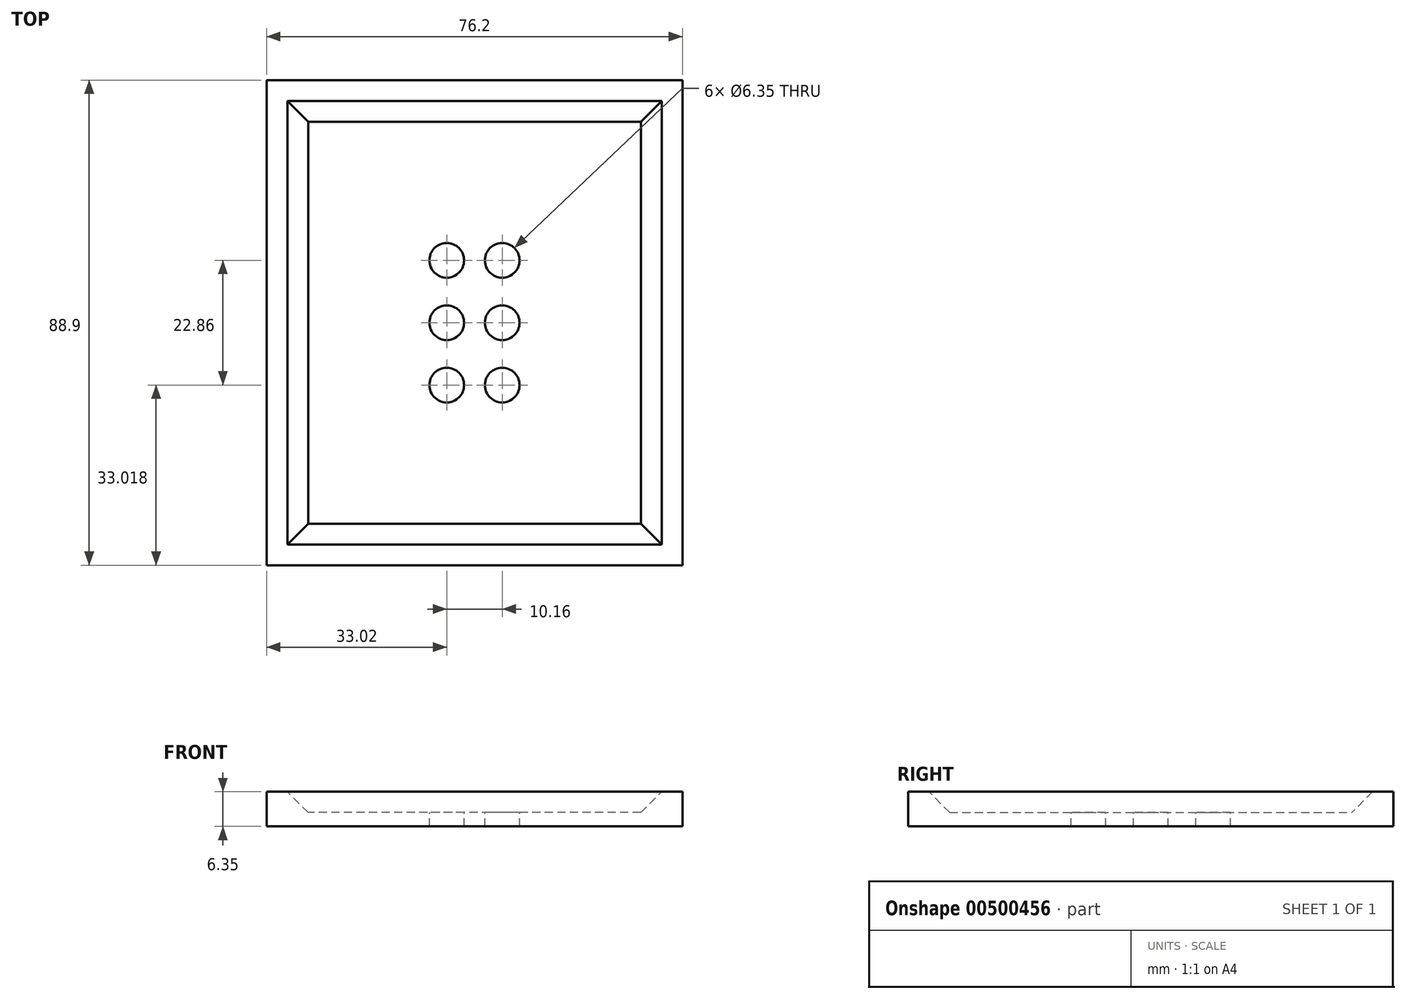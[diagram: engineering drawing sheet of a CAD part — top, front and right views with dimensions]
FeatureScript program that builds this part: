
annotation { "Feature Type Name" : "Feature", "Feature Type Description" : "" }
export const myFeature = defineFeature(function(context is Context, id is Id, definition is map)
    precondition{}
    {
        {
            var Q0;
            Q0=qCreatedBy(makeId("Right.planeOp"),FACE);
            var sketch = newSketch(context, id + "F0", { "sketchPlane" : qUnion([Q0])});
            skLineSegment(sketch, "E0.bottom", {"start": v(-32.26, 2.86) * mm, "end": v(56.64, 2.86) * mm});
            skLineSegment(sketch, "E0.top", {"start": v(-32.26, -3.49) * mm, "end": v(56.64, -3.49) * mm});
            skLineSegment(sketch, "E0.left", {"start": v(-32.26, 2.86) * mm, "end": v(-32.26, -3.49) * mm});
            skLineSegment(sketch, "E0.right", {"start": v(56.64, 2.86) * mm, "end": v(56.64, -3.49) * mm});
            skSolve(sketch);
        }
        {
            var Q0;
            Q0=makeQuery(id+"F0.imprint","IMPRINT",FACE,{"disambiguationData":[TD([[makeQuery(id+"F0.imprint","IMPRINT",EDGE,{"derivedFrom":sQuery(id+"F0.wireOp",EDGE,"E0.bottom")}),-1.0]])]});
            extrude(context, id + "F1", {"entities" : qUnion([Q0]), "depth" : 76.2 * mm});
        }
        {
            var Q0;
            Q0=makeQuery(id+"F1.opExtrude","SWEPT_FACE",FACE,{"disambiguationData":[OSD([sQuery(id+"F0.wireOp",EDGE,"E0.bottom")])]});
            shell(context, id + "F2", {"entities" : qUnion([Q0]), "thickness" : 2.54 * mm});
        }
        {
            var Q0;
            Q0=makeQuery(id+"F2.opShell","OFFSET_FACE",FACE,{"disambiguationData":[OSD([sQuery(id+"F0.wireOp",EDGE,"E0.top")])]});
            chamfer(context, id + "F3", {"entities" : qUnion([Q0]), "width" : 5.08 * mm, "tangentPropagation" : true});
        }
        {
            var Q0;
            Q0=makeQuery(id+"F2.opShell","OFFSET_FACE",FACE,{"disambiguationData":[OSD([sQuery(id+"F0.wireOp",EDGE,"E0.top")])]});
            var sketch = newSketch(context, id + "F4", { "sketchPlane" : qUnion([Q0])});
            skCircle(sketch, "E1", {"center": v(33.02, 23.62) * mm, "radius": 2.54 * mm});
            skCircle(sketch, "E2", {"center": v(43.18, 23.62) * mm, "radius": 2.54 * mm});
            skCircle(sketch, "E3", {"center": v(33.02, 12.19) * mm, "radius": 2.54 * mm});
            skCircle(sketch, "E4", {"center": v(43.18, 12.19) * mm, "radius": 2.54 * mm});
            skCircle(sketch, "E5", {"center": v(43.18, 0.76) * mm, "radius": 2.54 * mm});
            skCircle(sketch, "E6", {"center": v(33.02, 0.76) * mm, "radius": 2.54 * mm});
            skSolve(sketch);
        }
        {
            var Q0;
            Q0=sQuery(id+"F4.wireOp",VERTEX,"E1.center");
            var Q1;
            Q1=sQuery(id+"F4.wireOp",VERTEX,"E2.center");
            var Q2;
            Q2=sQuery(id+"F4.wireOp",VERTEX,"E4.center");
            var Q3;
            Q3=sQuery(id+"F4.wireOp",VERTEX,"E3.center");
            var Q4;
            Q4=sQuery(id+"F4.wireOp",VERTEX,"E6.center");
            var Q5;
            Q5=sQuery(id+"F4.wireOp",VERTEX,"E5.center");
            var Q6;
            Q6=makeQuery(id+"F1.opExtrude","SWEPT_BODY",BODY,{"disambiguationData":[OSD([sQuery(id+"F0.wireOp",EDGE,"E0.bottom"),sQuery(id+"F0.wireOp",EDGE,"E0.top"),sQuery(id+"F0.wireOp",EDGE,"E0.left"),sQuery(id+"F0.wireOp",EDGE,"E0.right")])]});
            hole(context, id + "F5", {"style" : HoleStyle.SIMPLE, "endStyle" : HoleEndStyle.BLIND, "holeDiameter" : 6.35 * mm, "holeDepth" : 12.7 * mm, "isTappedThrough" : true, "tappedDepth" : 12.7 * mm, "tapClearance" : 3, "locations" : qUnion([Q0, Q1, Q2, Q3, Q4, Q5]), "scope" : qUnion([Q6])});
        }
    });
